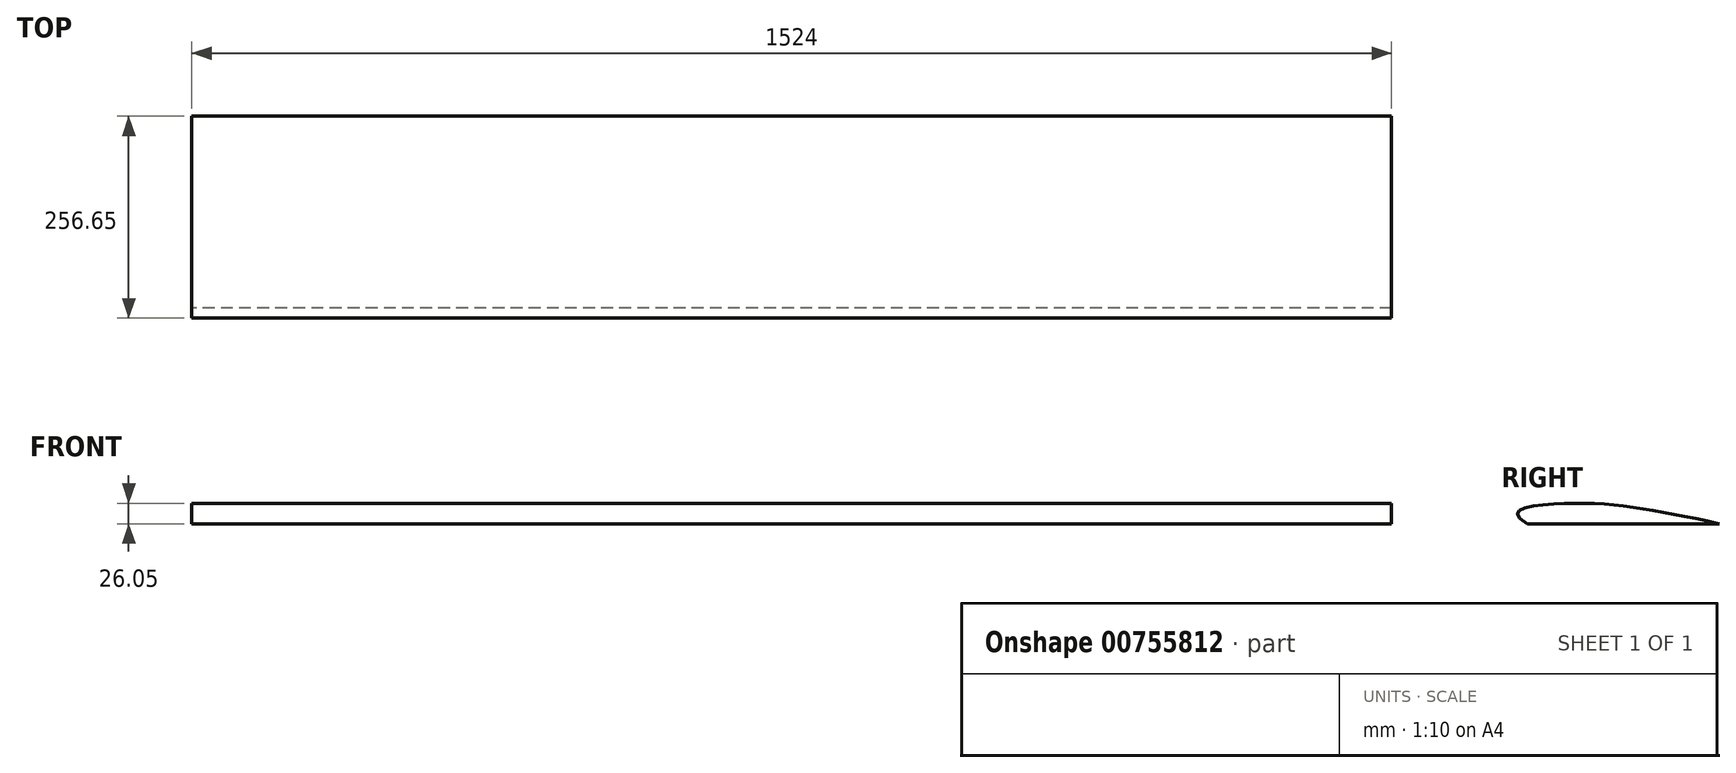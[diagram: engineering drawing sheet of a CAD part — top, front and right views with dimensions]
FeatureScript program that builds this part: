
annotation { "Feature Type Name" : "Feature", "Feature Type Description" : "" }
export const myFeature = defineFeature(function(context is Context, id is Id, definition is map)
    precondition{}
    {
        {
            var Q0;
            Q0=qCreatedBy(makeId("Right.planeOp"),FACE);
            var sketch = newSketch(context, id + "F0", { "sketchPlane" : qUnion([Q0])});
            skLineSegment(sketch, "E0", {"start": v(-43.35, 0) * mm, "end": v(200.49, 0) * mm});
            skFitSpline(sketch, "E1", {"points": [v(-43.35, 0) * mm, v(-6.03, 25.4) * mm, v(200.49, 0) * mm], "startDerivative": vector(-310.82, 178.28) * mm, "endDerivative": vector(365.92, -77.21) * mm});
            skSolve(sketch);
        }
        {
            var Q0;
            Q0=qSketchRegion(id+"F0",true);
            extrude(context, id + "F1", {"entities" : qUnion([Q0]), "depth" : 1524 * mm, "offsetDistance" : 25.4 * mm});
        }
    });
